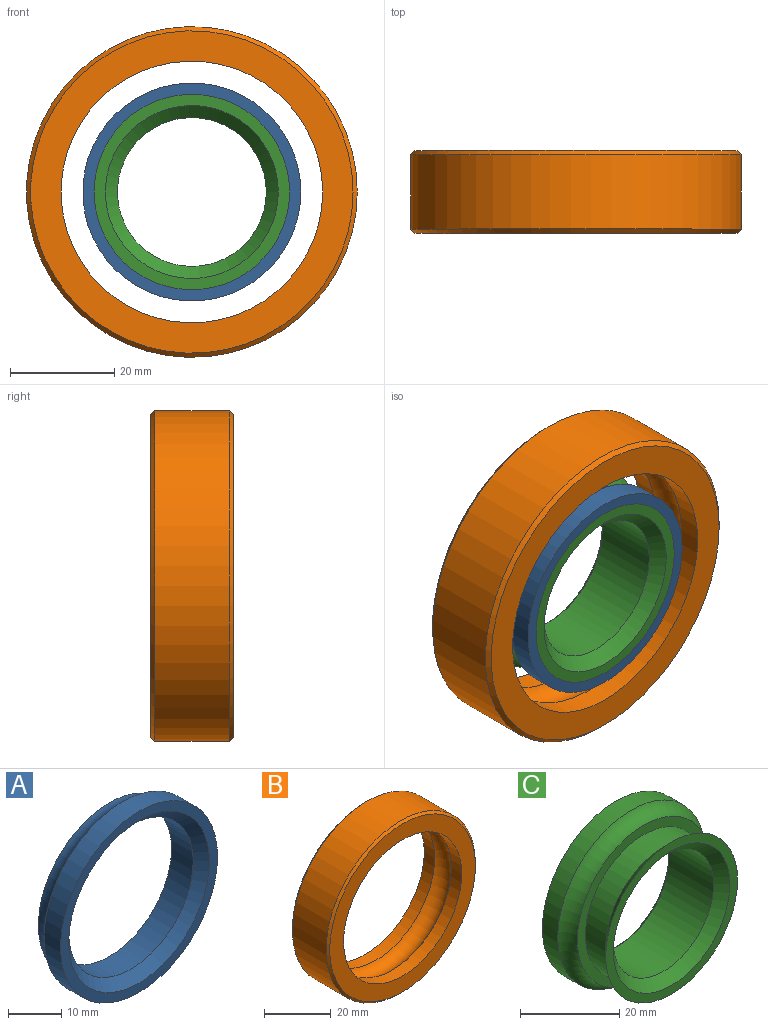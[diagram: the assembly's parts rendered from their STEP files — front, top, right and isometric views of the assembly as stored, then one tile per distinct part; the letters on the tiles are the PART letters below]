
ASSEMBLY  parts=3 mates=2
PART A: 6 faces, bbox 49.8x10.9x49.8 mm
  f0: plane 41.85x41.85mm, normal (0,-1,0), area 269.5mm2, adj f1,f5
  f1: cone r=18.76mm half-angle=45deg, axis (0,-1,0), area 339.7mm2, adj f0,f2
  f2: cylinder r=16.6mm len=33.2mm, axis (0,-1,0), area 602.5mm2, adj f1,f3
  f3: plane 37.83x37.83mm, normal (0,1,0), area 258.3mm2, adj f2,f4
  f4: torus R=23.02mm, axis (0,-1,0), area 523.3mm2, adj f3,f5
  f5: cylinder r=20.93mm len=41.85mm, axis (0,-1,0), area 579.8mm2, adj f0,f4
PART B: 8 faces, bbox 63.5x15.9x63.5 mm
  f0: cone r=31.75mm half-angle=45deg, axis (0,1,0), area 221.1mm2, adj f1,f7
  f1: cylinder r=31.75mm len=63.5mm, axis (0,-1,0), area 2850.2mm2, adj f0,f2
  f2: cone r=30.96mm half-angle=45deg, axis (0,-1,0), area 221.1mm2, adj f1,f3
  f3: plane 61.91x61.91mm, normal (0,1,0), area 1029.4mm2, adj f2,f4
  f4: cylinder r=25.11mm len=50.22mm, axis (0,-1,0), area 695.8mm2, adj f3,f5
  f5: torus R=23.02mm, axis (0,-1,0), area 1410.3mm2, adj f4,f6
  f6: cylinder r=25.11mm len=50.22mm, axis (0,-1,0), area 695.8mm2, adj f5,f7
  f7: plane 61.91x61.91mm, normal (0,-1,0), area 1029.4mm2, adj f0,f6
PART C: 10 faces, bbox 49.8x15.9x49.8 mm
  f0: plane 37.53x37.53mm, normal (0,-1,0), area 240.2mm2, adj f1,f9
  f1: cone r=16.6mm half-angle=45deg, axis (0,-1,0), area 339.7mm2, adj f0,f2
  f2: cylinder r=16.6mm len=33.2mm, axis (0,-1,0), area 602.5mm2, adj f1,f3
  f3: plane 37.83x37.83mm, normal (0,-1,0), area 258.3mm2, adj f2,f4
  f4: torus R=23.02mm, axis (0,-1,0), area 523.3mm2, adj f3,f5
  f5: cylinder r=20.93mm len=41.85mm, axis (0,-1,0), area 579.8mm2, adj f4,f6
  f6: plane 41.85x41.85mm, normal (0,1,0), area 661.1mm2, adj f5,f7
  f7: cone r=14.29mm half-angle=45deg, axis (0,1,0), area 103.6mm2, adj f6,f8
  f8: cylinder r=14.29mm len=28.58mm, axis (0,-1,0), area 1146.1mm2, adj f7,f9
  f9: cone r=16.6mm half-angle=45deg, axis (0,-1,0), area 317.6mm2, adj f0,f8
PLACE A t=(-0.25,-0.04,0.17)mm
PLACE B t=(-0.25,-0.04,0.17)mm
PLACE C t=(-0.25,-0.04,0.17)mm fixed
MATE fastened B.f0 <-> C.f1  axis (0,1,0) through (-0.25,7.9,0.17)mm
MATE fastened C.f1 <-> A.f1  axis (0,-1,0) through (-0.25,-0.04,0.17)mm
